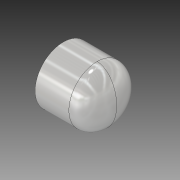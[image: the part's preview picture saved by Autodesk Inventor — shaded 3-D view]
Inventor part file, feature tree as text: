
AUTODESK INVENTOR PART (.ipt)
format: ipt  version: 2018 (Build 220112000, 112)  size: 172,032 bytes
history: native  units: in
note: dims shown in document units (in); Inventor stores cm internally (conversion verified against a paired STEP export)
features: revolve x1
ambient origin geometry x8: Origin, YZ Plane, XZ Plane, XY Plane, X Axis, Y Axis, Z Axis, Center Point
bodies: Solid1 (feature_tree)
feature tree (1):
  revolve  "Revolve1"  [1 undecoded]
note: 1 required parameter value undecoded (feature->parameter linkage not recoverable at this tier; creation-order binding heuristic only, values carry confidence <= 0.55)
